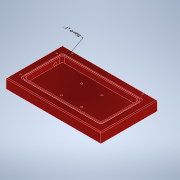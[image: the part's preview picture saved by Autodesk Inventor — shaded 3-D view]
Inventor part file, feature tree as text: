
AUTODESK INVENTOR PART (.ipt)
format: ipt  version: 2022 (Build 260153000, 153)  size: 231,424 bytes
history: native  units: mm
features: sketch x6, extrude x3, hole x3, other x2, chamfer x1
ambient origin geometry x8: Origin, YZ Plane, XZ Plane, XY Plane, X Axis, Y Axis, Z Axis, Center Point
bodies: Volumenkörper1 (feature_tree)
feature tree (15):
  other  "Annotations"
  extrude  "Extrusion1"  Depth=139.7mm
  extrude  "Extrusion2"  Depth=190.5mm
  chamfer  "Fase1"  Distance=14.0mm
  sketch  "Skizze4"  dims[d7=95.25mm d8=14.0mm d9=0.0mm]
  hole  "Bohrung7"  [1 undecoded]
  hole  "Hole9"  [1 undecoded]
  extrude  "Extrusion5"  Depth=6.924mm
  hole  "Hole10"  [1 undecoded]
  sketch  "Skizze1"  dims[d0=234.95mm d2=139.7mm]
  sketch  "Skizze2"  dims[d3=26.0mm d4=0.0mm d5=190.5mm]
  sketch  "Sketch13"  dims[d11=2.0mm d12=2.0mm d13=45.0deg d14=8.0mm]
  sketch  "Sketch14"  dims[d15=30.0mm d16=30.0mm]
  sketch  "Sketch15"  dims[d17=8.0mm d18=8.0mm d19=30.0mm d28=30.0mm d29=8.0mm d30=4.0mm d31=4.0mm d32=4.0mm d37=4.0mm d153=25.0mm d154=25.0mm d155=11.0mm d158=11.0mm d159=6.0mm d160=30.0mm d161=30.0mm d162=6.0mm d169=3.242mm d170=6.0mm d171=8.0mm d172=4.6mm d173=14.3117mm d174=20.0mm d175=20.594885mm d199=4.5mm d200=8.608mm d201=12.6mm d202=2.0mm d203=90.0deg d204=8.0mm d205=20.594885mm d216=6.35mm d219=50.0mm d220=50.0mm d221=2.54mm d222=2.54mm d223=6.35mm d224=2.921mm d225=2.921mm d226=6.35mm d227=2.032mm d228=0.0mm d230=16.0mm d231=40.0mm d232=7.9502mm d233=6.924mm d234=0.624793mm d235=8.304022mm d236=4.0mm d237=2.0mm d238=90.0deg d239=8.0mm d240=20.594885mm d229=0.361148mm]
  other  "Leader Text 1"
note: 3 required parameter values undecoded (feature->parameter linkage not recoverable at this tier; creation-order binding heuristic only, values carry confidence <= 0.55)
